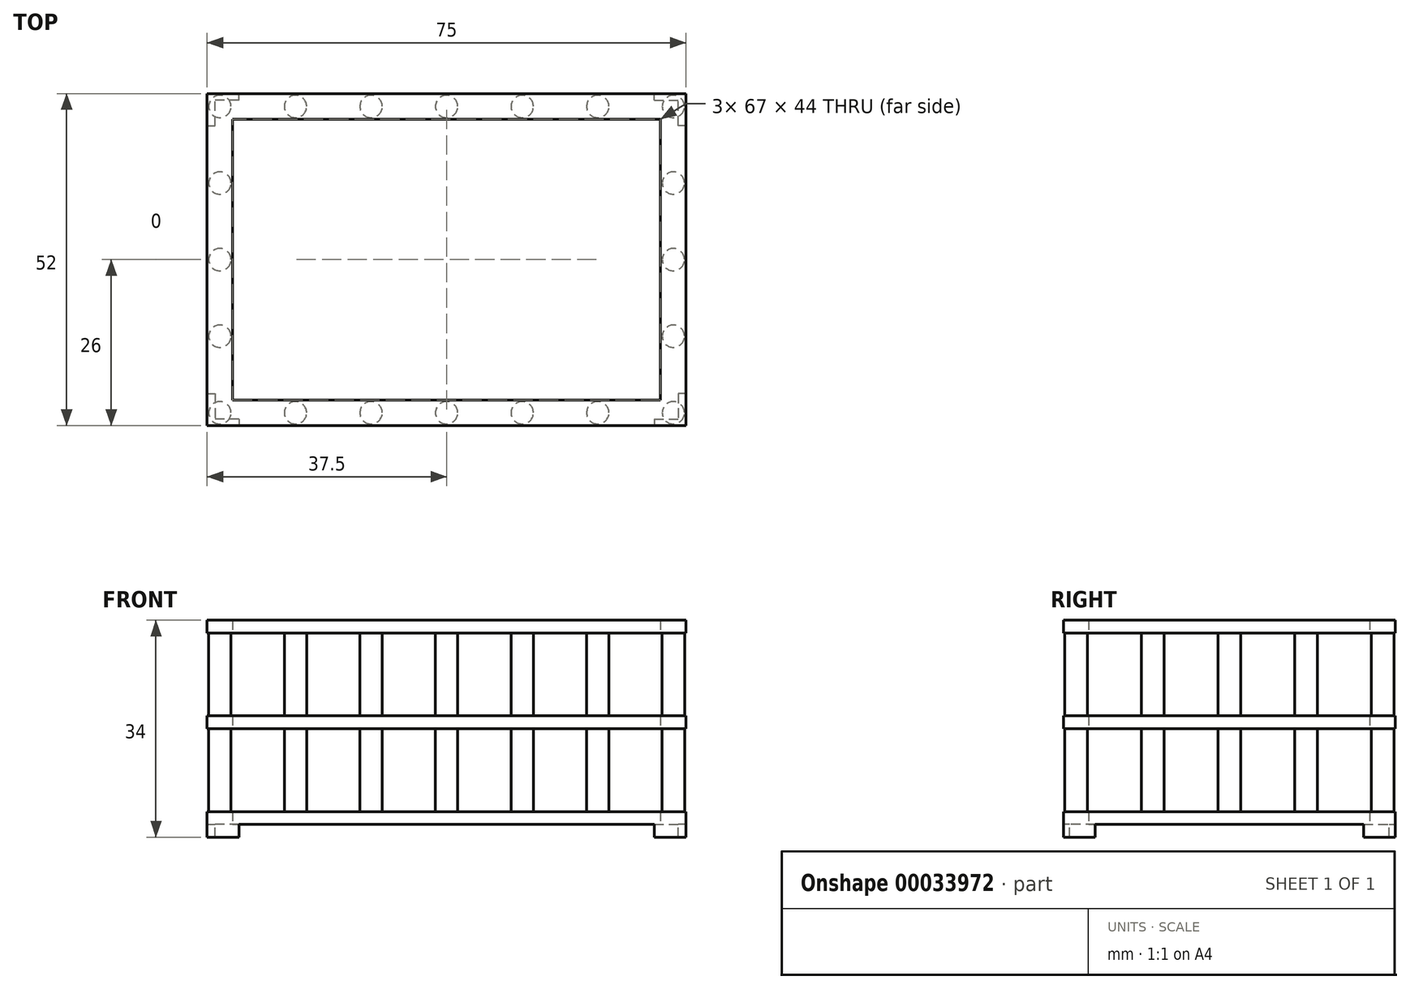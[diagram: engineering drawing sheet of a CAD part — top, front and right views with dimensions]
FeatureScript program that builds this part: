
annotation { "Feature Type Name" : "Feature", "Feature Type Description" : "" }
export const myFeature = defineFeature(function(context is Context, id is Id, definition is map)
    precondition{}
    {
        {
            var Q0;
            Q0=qCreatedBy(makeId("Top.planeOp"),FACE);
            var sketch = newSketch(context, id + "F0", { "sketchPlane" : qUnion([Q0])});
            skLineSegment(sketch, "E0.rect.bottom", {"start": v(-33.5, -22) * mm, "end": v(33.5, -22) * mm});
            skLineSegment(sketch, "E0.rect.top", {"start": v(-33.5, 22) * mm, "end": v(33.5, 22) * mm});
            skLineSegment(sketch, "E0.rect.left", {"start": v(-33.5, -22) * mm, "end": v(-33.5, 22) * mm});
            skLineSegment(sketch, "E0.rect.right", {"start": v(33.5, -22) * mm, "end": v(33.5, 22) * mm});
            skPoint(sketch, "E0.rect.middle", {"position": v(0, 0) * mm});
            skLineSegment(sketch, "E1.rect.bottom", {"start": v(-37.5, -26) * mm, "end": v(37.5, -26) * mm});
            skLineSegment(sketch, "E1.rect.top", {"start": v(-37.5, 26) * mm, "end": v(37.5, 26) * mm});
            skLineSegment(sketch, "E1.rect.left", {"start": v(-37.5, -26) * mm, "end": v(-37.5, 26) * mm});
            skLineSegment(sketch, "E1.rect.right", {"start": v(37.5, -26) * mm, "end": v(37.5, 26) * mm});
            skLineSegment(sketch, "E2.rect.bottom", {"start": v(-36.5, -25) * mm, "end": v(36.5, -25) * mm, "construction": true});
            skLineSegment(sketch, "E2.rect.top", {"start": v(-36.5, 25) * mm, "end": v(36.5, 25) * mm, "construction": true});
            skLineSegment(sketch, "E2.rect.left", {"start": v(-36.5, -25) * mm, "end": v(-36.5, 25) * mm, "construction": true});
            skLineSegment(sketch, "E2.rect.right", {"start": v(36.5, -25) * mm, "end": v(36.5, 25) * mm, "construction": true});
            skLineSegment(sketch, "E3.bottom", {"start": v(-37.5, 26) * mm, "end": v(-36.5, 26) * mm});
            skLineSegment(sketch, "E3.top", {"start": v(-37.5, 21) * mm, "end": v(-36.5, 21) * mm});
            skLineSegment(sketch, "E3.left", {"start": v(-37.5, 26) * mm, "end": v(-37.5, 21) * mm});
            skLineSegment(sketch, "E3.right", {"start": v(-36.5, 25) * mm, "end": v(-36.5, 21) * mm});
            skLineSegment(sketch, "E4.bottom", {"start": v(-37.5, 26) * mm, "end": v(-32.5, 26) * mm});
            skLineSegment(sketch, "E4.top", {"start": v(-36.5, 25) * mm, "end": v(-32.5, 25) * mm});
            skLineSegment(sketch, "E4.left", {"start": v(-37.5, 26) * mm, "end": v(-37.5, 25) * mm});
            skLineSegment(sketch, "E4.right", {"start": v(-32.5, 26) * mm, "end": v(-32.5, 25) * mm});
            skLineSegment(sketch, "E5.MirrorCS", {"start": v(32.5, 26) * mm, "end": v(32.5, 25) * mm});
            skLineSegment(sketch, "E6.MirrorCS", {"start": v(37.5, 21) * mm, "end": v(36.5, 21) * mm});
            skLineSegment(sketch, "E7.MirrorCS", {"start": v(37.5, 26) * mm, "end": v(37.5, 25) * mm});
            skLineSegment(sketch, "E8.MirrorCS", {"start": v(37.5, 26) * mm, "end": v(36.5, 26) * mm});
            skLineSegment(sketch, "E9.MirrorCS", {"start": v(36.5, 25) * mm, "end": v(32.5, 25) * mm});
            skLineSegment(sketch, "E10.MirrorCS", {"start": v(37.5, 26) * mm, "end": v(32.5, 26) * mm});
            skLineSegment(sketch, "E11.MirrorCS", {"start": v(36.5, 25) * mm, "end": v(36.5, 21) * mm});
            skLineSegment(sketch, "E12.MirrorCS", {"start": v(37.5, 26) * mm, "end": v(37.5, 21) * mm});
            skLineSegment(sketch, "E13.MirrorCS", {"start": v(33.5, 22) * mm, "end": v(-33.5, 22) * mm});
            skLineSegment(sketch, "E14.MirrorCS", {"start": v(36.5, 25) * mm, "end": v(-36.5, 25) * mm, "construction": true});
            skLineSegment(sketch, "E15.MirrorCS", {"start": v(37.5, 26) * mm, "end": v(-37.5, 26) * mm});
            skLineSegment(sketch, "E16.MirrorCS", {"start": v(-32.5, -26) * mm, "end": v(-32.5, -25) * mm});
            skLineSegment(sketch, "E17.MirrorCS", {"start": v(-37.5, -21) * mm, "end": v(-36.5, -21) * mm});
            skLineSegment(sketch, "E18.MirrorCS", {"start": v(-36.5, -25) * mm, "end": v(-36.5, -21) * mm});
            skLineSegment(sketch, "E19.MirrorCS", {"start": v(-37.5, -26) * mm, "end": v(-37.5, -21) * mm});
            skLineSegment(sketch, "E20.MirrorCS", {"start": v(-36.5, -25) * mm, "end": v(-32.5, -25) * mm});
            skLineSegment(sketch, "E21.MirrorCS", {"start": v(-37.5, -26) * mm, "end": v(-32.5, -26) * mm});
            skLineSegment(sketch, "E22.MirrorCS", {"start": v(37.5, -21) * mm, "end": v(36.5, -21) * mm});
            skLineSegment(sketch, "E23.MirrorCS", {"start": v(32.5, -26) * mm, "end": v(32.5, -25) * mm});
            skLineSegment(sketch, "E24.MirrorCS", {"start": v(36.5, -25) * mm, "end": v(32.5, -25) * mm});
            skLineSegment(sketch, "E25.MirrorCS", {"start": v(37.5, -26) * mm, "end": v(32.5, -26) * mm});
            skLineSegment(sketch, "E26.MirrorCS", {"start": v(37.5, -26) * mm, "end": v(37.5, -21) * mm});
            skLineSegment(sketch, "E27.MirrorCS", {"start": v(36.5, -25) * mm, "end": v(36.5, -21) * mm});
            skSolve(sketch);
        }
        {
            var Q0;
            Q0 = qSketchRegion(id + "F0", true);
            extrude(context, id + "F1", {"entities" : qUnion([Q0]), "depth" : 2 * mm});
        }
        {
            var Q0;
            Q0=makeQuery(id+"F1.opExtrude","SWEPT_BODY",BODY,{"disambiguationData":[OSD([sQuery(id+"F0.wireOp",EDGE,"E0.rect.bottom"),sQuery(id+"F0.wireOp",EDGE,"E0.rect.top"),sQuery(id+"F0.wireOp",EDGE,"E0.rect.left"),sQuery(id+"F0.wireOp",EDGE,"E0.rect.right"),sQuery(id+"F0.wireOp",EDGE,"E1.rect.bottom"),sQuery(id+"F0.wireOp",EDGE,"E1.rect.top"),sQuery(id+"F0.wireOp",EDGE,"E1.rect.left"),sQuery(id+"F0.wireOp",EDGE,"E1.rect.right")])]});
            transform(context, id + "F2", {"entities" : qUnion([Q0]), "transformType" : TransformType.TRANSLATION_3D, "dx" : 0 * mm, "dy" : 0 * mm, "dz" : 30 * mm, "makeCopy" : true});
        }
        {
            var Q0;
            Q0=makeQuery(id+"F1.opExtrude","SWEPT_BODY",BODY,{"disambiguationData":[OSD([sQuery(id+"F0.wireOp",EDGE,"E0.rect.bottom"),sQuery(id+"F0.wireOp",EDGE,"E0.rect.left"),sQuery(id+"F0.wireOp",EDGE,"E0.rect.right"),sQuery(id+"F0.wireOp",EDGE,"E1.rect.bottom"),sQuery(id+"F0.wireOp",EDGE,"E1.rect.left"),sQuery(id+"F0.wireOp",EDGE,"E1.rect.right"),sQuery(id+"F0.wireOp",EDGE,"E13.MirrorCS"),sQuery(id+"F0.wireOp",EDGE,"E15.MirrorCS"),sQuery(id+"F0.wireOp",EDGE,"E10.MirrorCS"),sQuery(id+"F0.wireOp",EDGE,"E12.MirrorCS"),sQuery(id+"F0.wireOp",EDGE,"E19.MirrorCS"),sQuery(id+"F0.wireOp",EDGE,"E21.MirrorCS"),sQuery(id+"F0.wireOp",EDGE,"E4.bottom"),sQuery(id+"F0.wireOp",EDGE,"E3.left"),sQuery(id+"F0.wireOp",EDGE,"E25.MirrorCS"),sQuery(id+"F0.wireOp",EDGE,"E26.MirrorCS")])]});
            transform(context, id + "F3", {"entities" : qUnion([Q0]), "transformType" : TransformType.TRANSLATION_3D, "dx" : 0 * mm, "dy" : 0 * mm, "dz" : 15 * mm, "makeCopy" : true});
        }
        {
            var Q0;
            Q0=qCreatedBy(makeId("Top.planeOp"),FACE);
            var sketch = newSketch(context, id + "F4", { "sketchPlane" : qUnion([Q0])});
            skLineSegment(sketch, "E28.rect.bottom", {"start": v(-35.5, 24) * mm, "end": v(35.5, 24) * mm, "construction": true});
            skLineSegment(sketch, "E28.rect.top", {"start": v(-35.5, -24) * mm, "end": v(35.5, -24) * mm, "construction": true});
            skLineSegment(sketch, "E28.rect.left", {"start": v(-35.5, 24) * mm, "end": v(-35.5, -24) * mm, "construction": true});
            skLineSegment(sketch, "E28.rect.right", {"start": v(35.5, 24) * mm, "end": v(35.5, -24) * mm, "construction": true});
            skCircle(sketch, "E29", {"center": v(-35.5, 24) * mm, "radius": 1.75 * mm});
            skCircle(sketch, "E30.1.0.0", {"center": v(-23.67, 24) * mm, "radius": 1.75 * mm});
            skCircle(sketch, "E30.2.0.0", {"center": v(-11.83, 24) * mm, "radius": 1.75 * mm});
            skCircle(sketch, "E30.3.0.0", {"center": v(0, 24) * mm, "radius": 1.75 * mm});
            skCircle(sketch, "E30.4.0.0", {"center": v(11.83, 24) * mm, "radius": 1.75 * mm});
            skCircle(sketch, "E30.5.0.0", {"center": v(23.67, 24) * mm, "radius": 1.75 * mm});
            skCircle(sketch, "E30.6.0.0", {"center": v(35.5, 24) * mm, "radius": 1.75 * mm});
            skLineSegment(sketch, "E30.direction1", {"start": v(-35.5, 24) * mm, "end": v(-23.67, 24) * mm, "construction": true});
            skLineSegment(sketch, "E31.direction1", {"start": v(-35.5, 24) * mm, "end": v(-35.5, 11.75) * mm, "construction": true});
            skLineSegment(sketch, "E32.MirrorCS", {"start": v(-35.5, -24) * mm, "end": v(-35.5, -11.75) * mm, "construction": true});
            skLineSegment(sketch, "E33.MirrorCS", {"start": v(-35.5, -24) * mm, "end": v(-35.5, 24) * mm, "construction": true});
            skLineSegment(sketch, "E34.MirrorCS", {"start": v(35.5, 24) * mm, "end": v(35.5, 11.75) * mm, "construction": true});
            skLineSegment(sketch, "E35.MirrorCS", {"start": v(35.5, -24) * mm, "end": v(35.5, 24) * mm, "construction": true});
            skLineSegment(sketch, "E36.MirrorCS", {"start": v(35.5, -24) * mm, "end": v(35.5, -11.75) * mm, "construction": true});
            skCircle(sketch, "E37.0.1.0", {"center": v(-35.5, 12) * mm, "radius": 1.75 * mm});
            skLineSegment(sketch, "E37.direction2", {"start": v(-35.5, 24) * mm, "end": v(-35.5, 12) * mm, "construction": true});
            skCircle(sketch, "E38.0.0.2", {"center": v(-35.5, 0) * mm, "radius": 1.75 * mm});
            skCircle(sketch, "E38.0.0.3", {"center": v(-35.5, -12) * mm, "radius": 1.75 * mm});
            skCircle(sketch, "E38.0.0.4", {"center": v(-35.5, -24) * mm, "radius": 1.75 * mm});
            skCircle(sketch, "E39.0.1.0", {"center": v(35.5, 12) * mm, "radius": 1.75 * mm});
            skCircle(sketch, "E39.0.2.0", {"center": v(35.5, 0) * mm, "radius": 1.75 * mm});
            skCircle(sketch, "E39.0.3.0", {"center": v(35.5, -12) * mm, "radius": 1.75 * mm});
            skCircle(sketch, "E39.0.4.0", {"center": v(35.5, -24) * mm, "radius": 1.75 * mm});
            skLineSegment(sketch, "E39.direction1", {"start": v(35.5, 24) * mm, "end": v(60.5, 24) * mm, "construction": true});
            skLineSegment(sketch, "E39.direction2", {"start": v(35.5, 24) * mm, "end": v(35.5, 12) * mm, "construction": true});
            skCircle(sketch, "E40.1.0.0", {"center": v(-23.67, -24) * mm, "radius": 1.75 * mm});
            skCircle(sketch, "E40.2.0.0", {"center": v(-11.83, -24) * mm, "radius": 1.75 * mm});
            skCircle(sketch, "E40.3.0.0", {"center": v(0, -24) * mm, "radius": 1.75 * mm});
            skCircle(sketch, "E40.4.0.0", {"center": v(11.83, -24) * mm, "radius": 1.75 * mm});
            skCircle(sketch, "E40.5.0.0", {"center": v(23.67, -24) * mm, "radius": 1.75 * mm});
            skLineSegment(sketch, "E40.direction1", {"start": v(-35.5, -24) * mm, "end": v(-23.67, -24) * mm, "construction": true});
            skSolve(sketch);
        }
        {
            var Q0;
            Q0 = qSketchRegion(id + "F4", true);
            extrude(context, id + "F5", {"entities" : qUnion([Q0]), "operationType" : NewBodyOperationType.ADD, "depth" : 30 * mm});
        }
        {
            var Q0;
            Q0=makeQuery(id+"F1.opExtrude","CAP_FACE",FACE,{"disambiguationData":[OSD([sQuery(id+"F0.wireOp",EDGE,"E0.rect.bottom"),sQuery(id+"F0.wireOp",EDGE,"E0.rect.left"),sQuery(id+"F0.wireOp",EDGE,"E0.rect.right"),sQuery(id+"F0.wireOp",EDGE,"E1.rect.bottom"),sQuery(id+"F0.wireOp",EDGE,"E1.rect.left"),sQuery(id+"F0.wireOp",EDGE,"E1.rect.right"),sQuery(id+"F0.wireOp",EDGE,"E13.MirrorCS"),sQuery(id+"F0.wireOp",EDGE,"E15.MirrorCS"),sQuery(id+"F0.wireOp",EDGE,"E10.MirrorCS"),sQuery(id+"F0.wireOp",EDGE,"E12.MirrorCS"),sQuery(id+"F0.wireOp",EDGE,"E19.MirrorCS"),sQuery(id+"F0.wireOp",EDGE,"E21.MirrorCS"),sQuery(id+"F0.wireOp",EDGE,"E4.bottom"),sQuery(id+"F0.wireOp",EDGE,"E3.left"),sQuery(id+"F0.wireOp",EDGE,"E25.MirrorCS"),sQuery(id+"F0.wireOp",EDGE,"E26.MirrorCS")])],"isStart":true});
            var sketch = newSketch(context, id + "F6", { "sketchPlane" : qUnion([Q0])});
            skLineSegment(sketch, "E41.rect.bottom", {"start": v(-35.8, -23) * mm, "end": v(33.76, -23) * mm, "construction": true});
            skLineSegment(sketch, "E41.rect.top", {"start": v(-35.8, 22) * mm, "end": v(33.76, 22) * mm, "construction": true});
            skLineSegment(sketch, "E41.rect.left", {"start": v(-35.8, -23) * mm, "end": v(-35.8, 22) * mm, "construction": true});
            skLineSegment(sketch, "E41.rect.right", {"start": v(33.76, -23) * mm, "end": v(33.76, 22) * mm, "construction": true});
            skLineSegment(sketch, "E42.rect.bottom", {"start": v(-37.5, -26.5) * mm, "end": v(37.76, -26.5) * mm, "construction": true});
            skLineSegment(sketch, "E42.rect.top", {"start": v(-37.5, 26) * mm, "end": v(37.76, 26) * mm, "construction": true});
            skLineSegment(sketch, "E42.rect.left", {"start": v(-37.5, -26.5) * mm, "end": v(-37.5, 26) * mm, "construction": true});
            skLineSegment(sketch, "E42.rect.right", {"start": v(37.76, -26.5) * mm, "end": v(37.76, 26) * mm, "construction": true});
            skLineSegment(sketch, "E43.rect.bottom", {"start": v(-36.24, -26) * mm, "end": v(36.76, -26) * mm, "construction": true});
            skLineSegment(sketch, "E43.rect.top", {"start": v(-36.24, 25) * mm, "end": v(36.76, 25) * mm, "construction": true});
            skLineSegment(sketch, "E43.rect.left", {"start": v(-36.24, -26) * mm, "end": v(-36.24, 25) * mm, "construction": true});
            skLineSegment(sketch, "E43.rect.right", {"start": v(36.76, -26) * mm, "end": v(36.76, 25) * mm, "construction": true});
            skLineSegment(sketch, "E44", {"start": v(-37.5, 26) * mm, "end": v(-37.5, 21) * mm});
            skLineSegment(sketch, "E45", {"start": v(-37.5, 21) * mm, "end": v(-36.24, 21) * mm});
            skLineSegment(sketch, "E46", {"start": v(-36.24, 21) * mm, "end": v(-36.24, 25) * mm});
            skLineSegment(sketch, "E47", {"start": v(-32.5, 25) * mm, "end": v(-32.5, 26) * mm});
            skLineSegment(sketch, "E48", {"start": v(-32.5, 26) * mm, "end": v(-37.5, 26) * mm});
            skLineSegment(sketch, "E49", {"start": v(-32.5, 25) * mm, "end": v(-36.24, 25) * mm});
            skSolve(sketch);
        }
        {
            var Q0;
            Q0=makeQuery(id+"F6.imprint","IMPRINT",FACE,{"disambiguationData":[TD([[makeQuery(id+"F6.imprint","IMPRINT",EDGE,{"derivedFrom":sQuery(id+"F6.wireOp",EDGE,"E44")}),1.0]])]});
            extrude(context, id + "F7", {"entities" : qUnion([Q0]), "depth" : 2 * mm});
        }
        {
            var Q0;
            Q0=makeQuery(id+"F7.opExtrude","SWEPT_BODY",BODY,{"disambiguationData":[OSD([sQuery(id+"F6.wireOp",EDGE,"E44"),sQuery(id+"F6.wireOp",EDGE,"E45"),sQuery(id+"F6.wireOp",EDGE,"E46"),sQuery(id+"F6.wireOp",EDGE,"E47"),sQuery(id+"F6.wireOp",EDGE,"E48"),sQuery(id+"F6.wireOp",EDGE,"E49")])]});
            var Q1;
            Q1=qCreatedBy(makeId("Right.planeOp"),FACE);
            mirror(context, id + "F8", {"entities" : qUnion([Q0]), "mirrorPlane" : qUnion([Q1])});
        }
        {
            var Q0;
            Q0=makeQuery(id+"F7.opExtrude","SWEPT_BODY",BODY,{"disambiguationData":[OSD([sQuery(id+"F6.wireOp",EDGE,"E44"),sQuery(id+"F6.wireOp",EDGE,"E45"),sQuery(id+"F6.wireOp",EDGE,"E46"),sQuery(id+"F6.wireOp",EDGE,"E47"),sQuery(id+"F6.wireOp",EDGE,"E48"),sQuery(id+"F6.wireOp",EDGE,"E49")])]});
            var Q1;
            Q1=makeQuery(id+"F8.opPattern","COPY",BODY,{"derivedFrom":makeQuery(id+"F7.opExtrude","SWEPT_BODY",BODY,{"disambiguationData":[OSD([sQuery(id+"F6.wireOp",EDGE,"E44"),sQuery(id+"F6.wireOp",EDGE,"E45"),sQuery(id+"F6.wireOp",EDGE,"E46"),sQuery(id+"F6.wireOp",EDGE,"E47"),sQuery(id+"F6.wireOp",EDGE,"E48"),sQuery(id+"F6.wireOp",EDGE,"E49")])]}),"instanceName":"1"});
            var Q2;
            Q2=qCreatedBy(makeId("Front.planeOp"),FACE);
            mirror(context, id + "F9", {"operationType" : NewBodyOperationType.ADD, "entities" : qUnion([Q0, Q1]), "mirrorPlane" : qUnion([Q2])});
        }
    });
